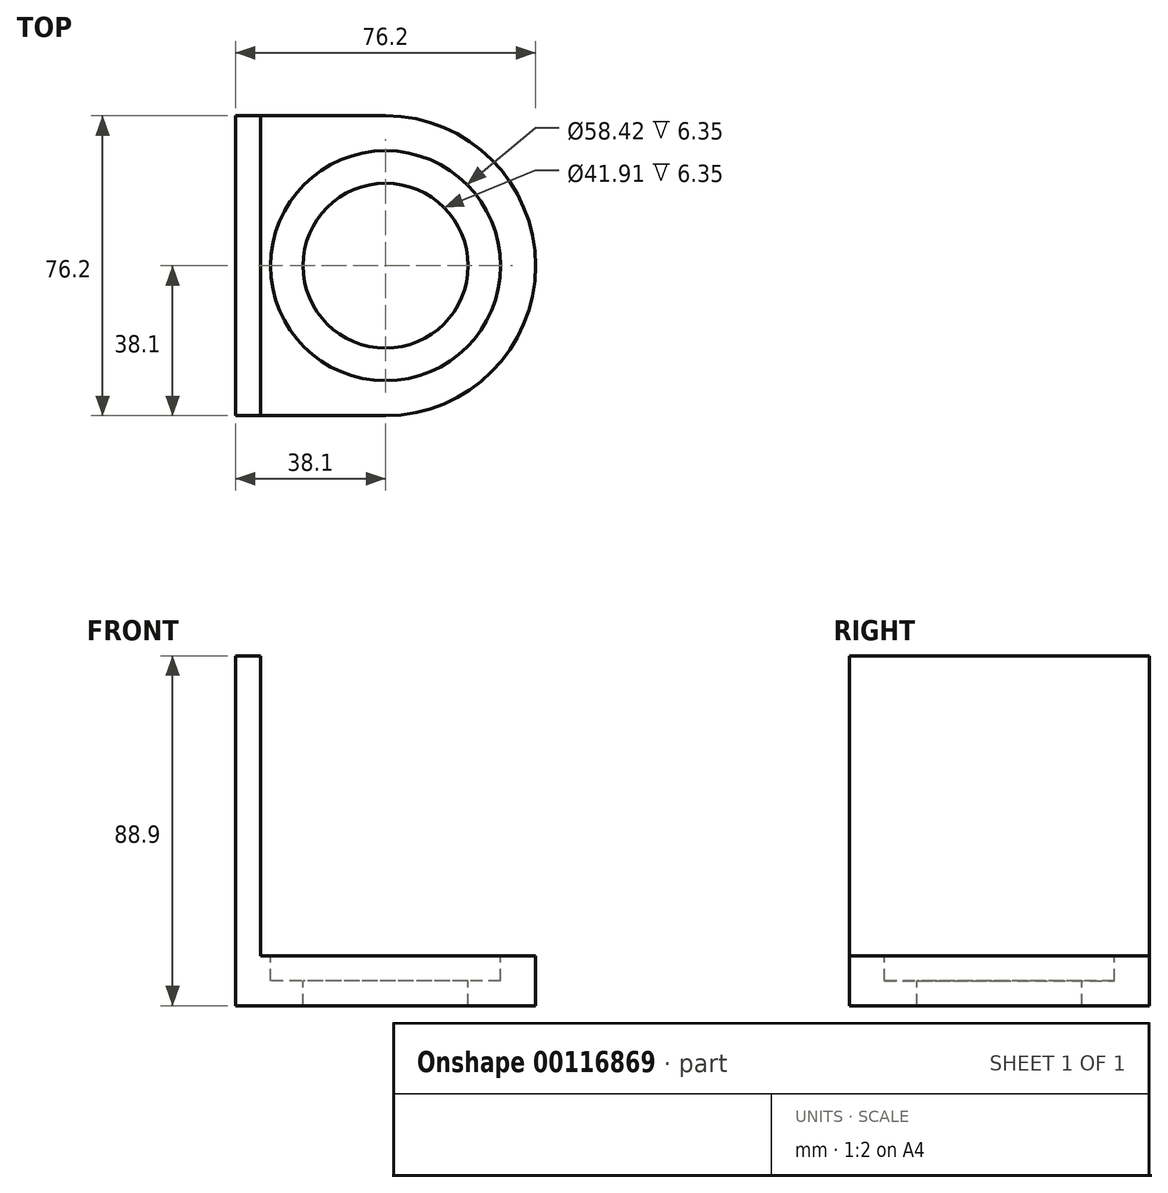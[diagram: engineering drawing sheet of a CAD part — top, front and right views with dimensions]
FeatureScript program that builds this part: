
annotation { "Feature Type Name" : "Feature", "Feature Type Description" : "" }
export const myFeature = defineFeature(function(context is Context, id is Id, definition is map)
    precondition{}
    {
        {
            var Q0;
            Q0=qCreatedBy(makeId("Top.planeOp"),FACE);
            var sketch = newSketch(context, id + "F0", { "sketchPlane" : qUnion([Q0])});
            skLineSegment(sketch, "E0.bottom", {"start": v(0, 38.1) * mm, "end": v(-38.1, 38.1) * mm});
            skLineSegment(sketch, "E0.top", {"start": v(0, -38.1) * mm, "end": v(-38.1, -38.1) * mm});
            skLineSegment(sketch, "E0.right", {"start": v(-38.1, 38.1) * mm, "end": v(-38.1, -38.1) * mm});
            skPoint(sketch, "E0.middle", {"position": v(0, 0) * mm});
            skArc(sketch, "E1", {"start": v(0, 38.1) * mm, "mid": v(38.1, 0) * mm, "end": v(0, -38.1) * mm});
            skPoint(sketch, "E2", {"position": v(0, 38.1) * mm});
            skPoint(sketch, "E3", {"position": v(0, -38.1) * mm});
            skPoint(sketch, "E4.orphan", {"position": v(38.1, 38.1) * mm});
            skPoint(sketch, "E5.orphan", {"position": v(38.1, -38.1) * mm});
            skSolve(sketch);
        }
        {
            var Q0;
            Q0 = qSketchRegion(id + "F0", true);
            extrude(context, id + "F1", {"entities" : qUnion([Q0]), "depth" : 12.7 * mm});
        }
        {
            var Q0;
            Q0=makeQuery(id+"F1.opExtrude","CAP_FACE",FACE,{"disambiguationData":[OSD([sQuery(id+"F0.wireOp",EDGE,"E0.bottom"),sQuery(id+"F0.wireOp",EDGE,"E0.top"),sQuery(id+"F0.wireOp",EDGE,"E0.right"),sQuery(id+"F0.wireOp",EDGE,"E1")])],"isStart":false});
            var sketch = newSketch(context, id + "F2", { "sketchPlane" : qUnion([Q0])});
            skCircle(sketch, "E6", {"center": v(0, 0) * mm, "radius": 29.21 * mm});
            skSolve(sketch);
        }
        {
            var Q0;
            Q0 = qSketchRegion(id + "F2", true);
            extrude(context, id + "F3", {"entities" : qUnion([Q0]), "operationType" : NewBodyOperationType.REMOVE, "oppositeDirection" : true, "depth" : 6.35 * mm});
        }
        {
            var Q0;
            Q0=makeQuery(id+"F3.boolean.opBoolean","COPY",FACE,{"derivedFrom":makeQuery(id+"F3.opExtrude","CAP_FACE",FACE,{"disambiguationData":[OSD([sQuery(id+"F2.wireOp",EDGE,"E6")])],"isStart":false})});
            var sketch = newSketch(context, id + "F4", { "sketchPlane" : qUnion([Q0])});
            skCircle(sketch, "E7", {"center": v(0, 0) * mm, "radius": 20.96 * mm});
            skSolve(sketch);
        }
        {
            var Q0;
            Q0 = qSketchRegion(id + "F4", true);
            extrude(context, id + "F5", {"entities" : qUnion([Q0]), "operationType" : NewBodyOperationType.REMOVE, "oppositeDirection" : true, "depth" : 6.35 * mm});
        }
        {
            var Q0;
            Q0=makeQuery(id+"F1.opExtrude","CAP_FACE",FACE,{"disambiguationData":[OSD([sQuery(id+"F0.wireOp",EDGE,"E0.bottom"),sQuery(id+"F0.wireOp",EDGE,"E0.top"),sQuery(id+"F0.wireOp",EDGE,"E0.right"),sQuery(id+"F0.wireOp",EDGE,"E1")])],"isStart":false});
            var sketch = newSketch(context, id + "F6", { "sketchPlane" : qUnion([Q0])});
            skLineSegment(sketch, "E8.bottom", {"start": v(-38.1, 38.1) * mm, "end": v(-31.75, 38.1) * mm});
            skLineSegment(sketch, "E8.top", {"start": v(-38.1, -38.1) * mm, "end": v(-31.75, -38.1) * mm});
            skLineSegment(sketch, "E8.left", {"start": v(-38.1, 38.1) * mm, "end": v(-38.1, -38.1) * mm});
            skLineSegment(sketch, "E8.right", {"start": v(-31.75, 38.1) * mm, "end": v(-31.75, -38.1) * mm});
            skSolve(sketch);
        }
        {
            var Q0;
            Q0 = qSketchRegion(id + "F6", true);
            extrude(context, id + "F7", {"entities" : qUnion([Q0]), "operationType" : NewBodyOperationType.ADD, "depth" : 76.2 * mm});
        }
    });
